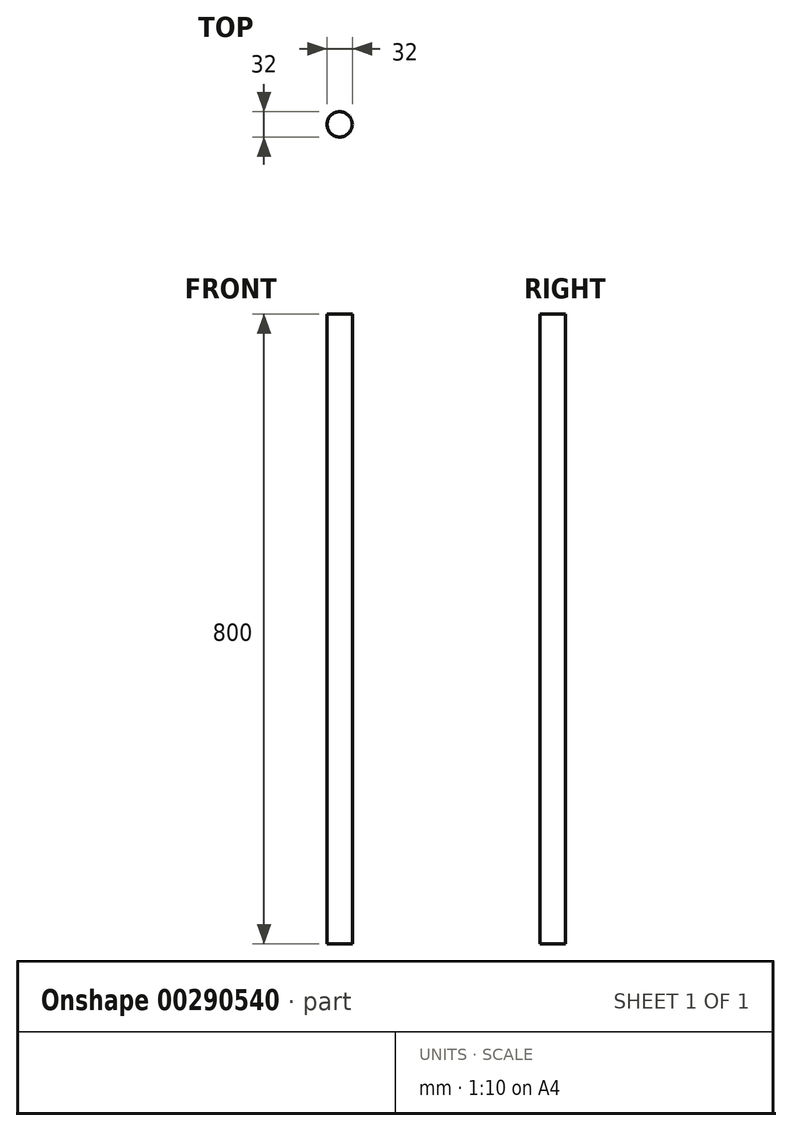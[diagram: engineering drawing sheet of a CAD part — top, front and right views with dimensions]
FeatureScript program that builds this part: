
annotation { "Feature Type Name" : "Feature", "Feature Type Description" : "" }
export const myFeature = defineFeature(function(context is Context, id is Id, definition is map)
    precondition{}
    {
        {
            var Q0;
            Q0=qCreatedBy(makeId("Top.planeOp"),FACE);
            var sketch = newSketch(context, id + "F0", { "sketchPlane" : qUnion([Q0])});
            skCircle(sketch, "E0", {"center": v(0, 0) * mm, "radius": 16 * mm});
            skSolve(sketch);
        }
        {
            var Q0;
            Q0=makeQuery(id+"F0.imprint","IMPRINT",FACE,{"disambiguationData":[TD([[makeQuery(id+"F0.imprint","IMPRINT",EDGE,{"derivedFrom":sQuery(id+"F0.wireOp",EDGE,"E0")}),1.0]])]});
            extrude(context, id + "F1", {"entities" : qUnion([Q0]), "depth" : 800 * mm});
        }
    });
